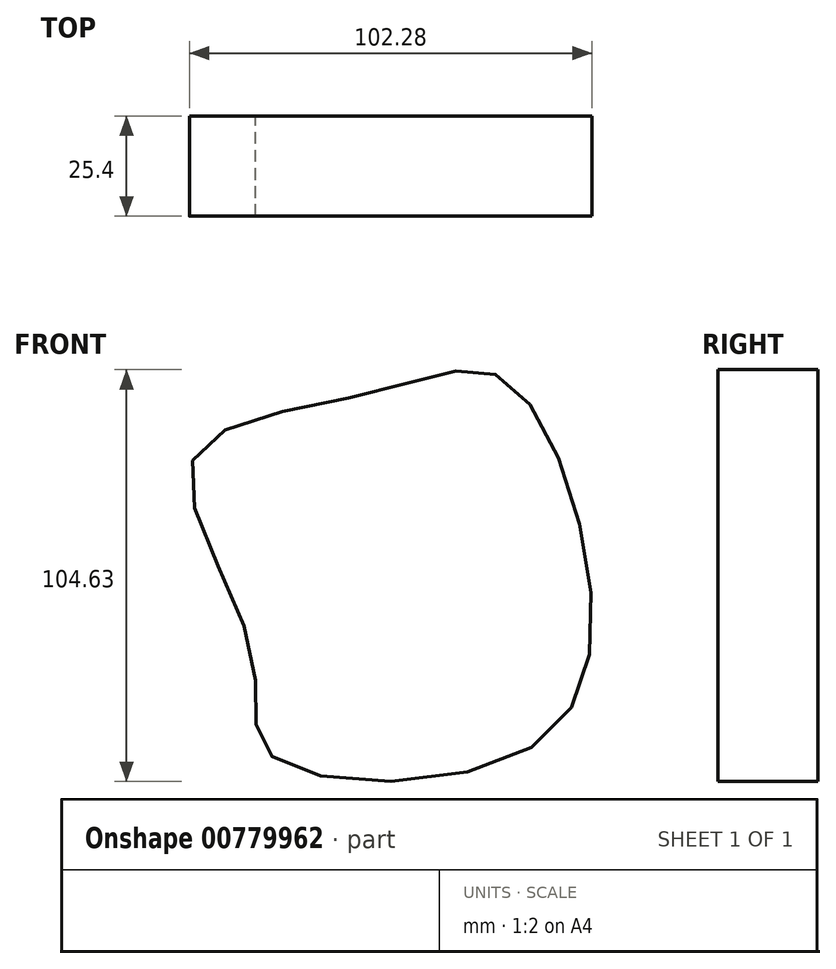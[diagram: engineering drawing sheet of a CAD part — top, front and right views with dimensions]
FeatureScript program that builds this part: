
annotation { "Feature Type Name" : "Feature", "Feature Type Description" : "" }
export const myFeature = defineFeature(function(context is Context, id is Id, definition is map)
    precondition{}
    {
        {
            var Q0;
            Q0=qCreatedBy(makeId("Front.planeOp"),FACE);
            var sketch = newSketch(context, id + "F0", { "sketchPlane" : qUnion([Q0])});
            skFitSpline(sketch, "E0", {"points": [v(-46.2, 30.3) * mm, v(-31.04, -18.48) * mm, v(-26.24, -44.72) * mm, v(38.06, -43.6) * mm, v(54.7, 0) * mm, v(32.52, 51.37) * mm, v(0, 47.67) * mm, v(-46.2, 30.3) * mm]});
            skSolve(sketch);
        }
        {
            var Q0;
            Q0 = qSketchRegion(id + "F0", true);
            extrude(context, id + "F1", {"entities" : qUnion([Q0]), "depth" : 25.4 * mm, "offsetDistance" : 25.4 * mm});
        }
    });
